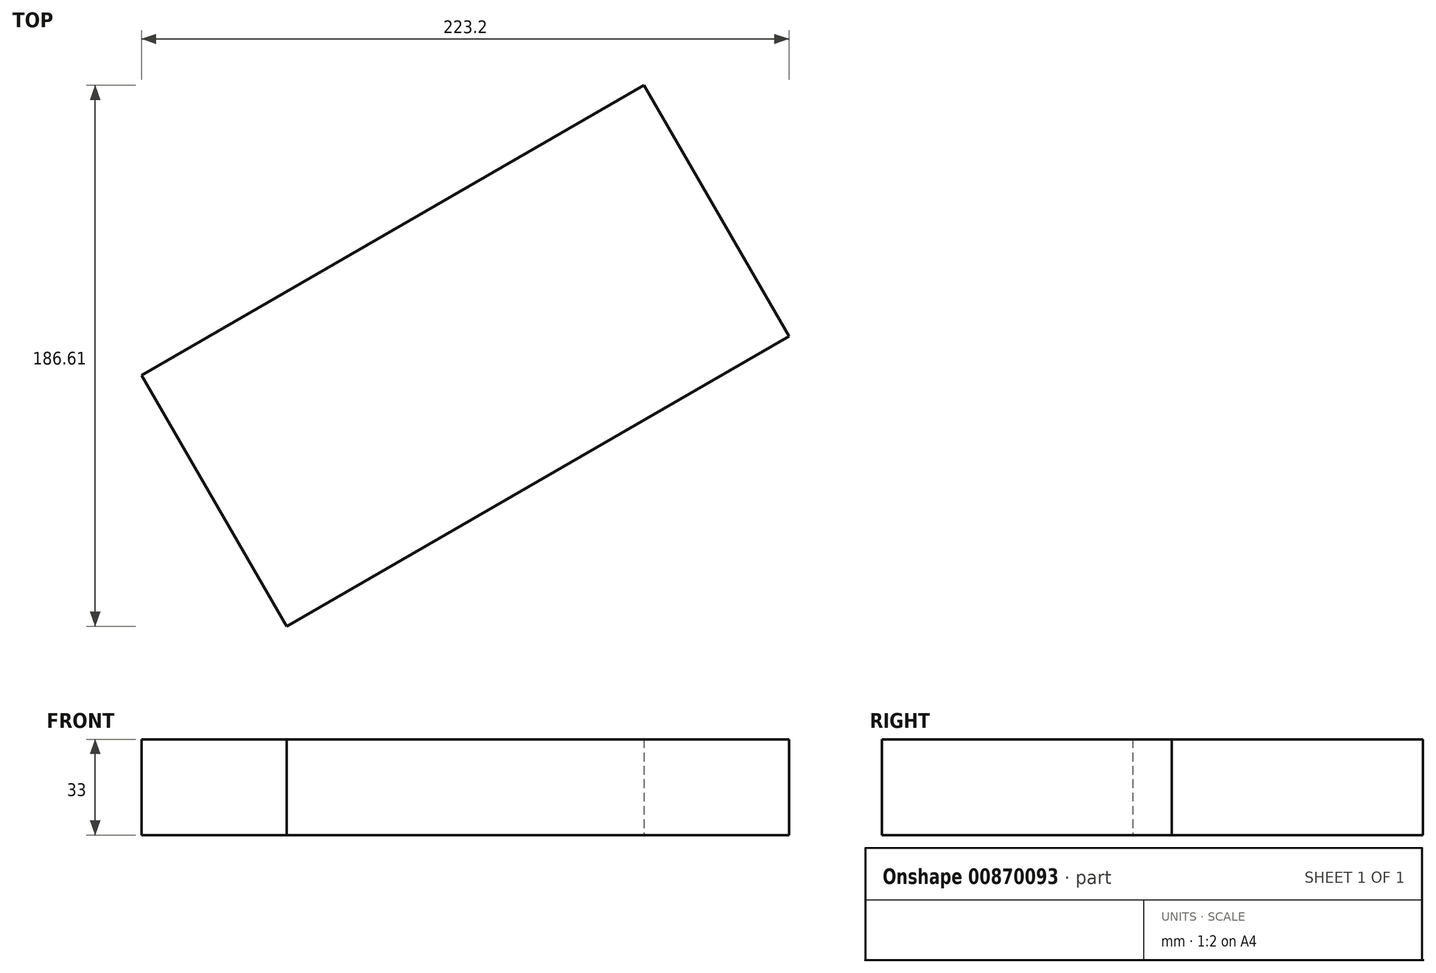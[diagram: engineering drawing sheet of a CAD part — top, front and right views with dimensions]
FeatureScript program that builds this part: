
annotation { "Feature Type Name" : "Feature", "Feature Type Description" : "" }
export const myFeature = defineFeature(function(context is Context, id is Id, definition is map)
    precondition{}
    {
        {
            var Q0;
            Q0=qCreatedBy(makeId("Top.planeOp"),FACE);
            var sketch = newSketch(context, id + "F0", { "sketchPlane" : qUnion([Q0])});
            skCircle(sketch, "E0.cCircle", {"center": v(0, 0) * mm, "radius": 106.8 * mm, "construction": true});
            skLineSegment(sketch, "E0.0", {"start": v(-0.07, -213.62) * mm, "end": v(-184.97, 106.87) * mm, "construction": true});
            skLineSegment(sketch, "E0.1", {"start": v(-184.97, 106.87) * mm, "end": v(185.03, 106.75) * mm, "construction": true});
            skLineSegment(sketch, "E0.2", {"start": v(185.03, 106.75) * mm, "end": v(-0.07, -213.62) * mm, "construction": true});
            skPoint(sketch, "E0.0.midPoint", {"position": v(-92.52, -53.38) * mm});
            skLineSegment(sketch, "E1.bottom", {"start": v(-129.06, -16.42) * mm, "end": v(44.14, 83.58) * mm});
            skLineSegment(sketch, "E1.top", {"start": v(-79.06, -103.03) * mm, "end": v(94.14, -3.03) * mm});
            skLineSegment(sketch, "E1.left", {"start": v(-129.06, -16.42) * mm, "end": v(-79.06, -103.03) * mm});
            skLineSegment(sketch, "E1.right", {"start": v(44.14, 83.58) * mm, "end": v(94.14, -3.03) * mm});
            skCircle(sketch, "E2", {"center": v(0, 0) * mm, "radius": 120 * mm, "construction": true});
            skLineSegment(sketch, "E3", {"start": v(-127.7, 120.04) * mm, "end": v(122.3, 119.96) * mm});
            skLineSegment(sketch, "E4", {"start": v(122.3, 119.96) * mm, "end": v(167.81, 50.58) * mm});
            skLineSegment(sketch, "E5", {"start": v(167.81, 50.58) * mm, "end": v(42.74, -165.89) * mm});
            skLineSegment(sketch, "E6", {"start": v(42.74, -165.89) * mm, "end": v(-40.1, -170.62) * mm});
            skLineSegment(sketch, "E7", {"start": v(-40.1, -170.62) * mm, "end": v(-165.04, 45.93) * mm});
            skLineSegment(sketch, "E8", {"start": v(-165.04, 45.93) * mm, "end": v(-127.7, 120.04) * mm});
            skSolve(sketch);
        }
        {
            var Q0;
            Q0=makeQuery(id+"F0.imprint","IMPRINT",FACE,{"disambiguationData":[TD([[makeQuery(id+"F0.imprint","IMPRINT",EDGE,{"derivedFrom":sQuery(id+"F0.wireOp",EDGE,"E1.bottom")}),-1.0]])]});
            extrude(context, id + "F1", {"entities" : qUnion([Q0]), "depth" : 33 * mm, "offsetDistance" : 25 * mm});
        }
    });
